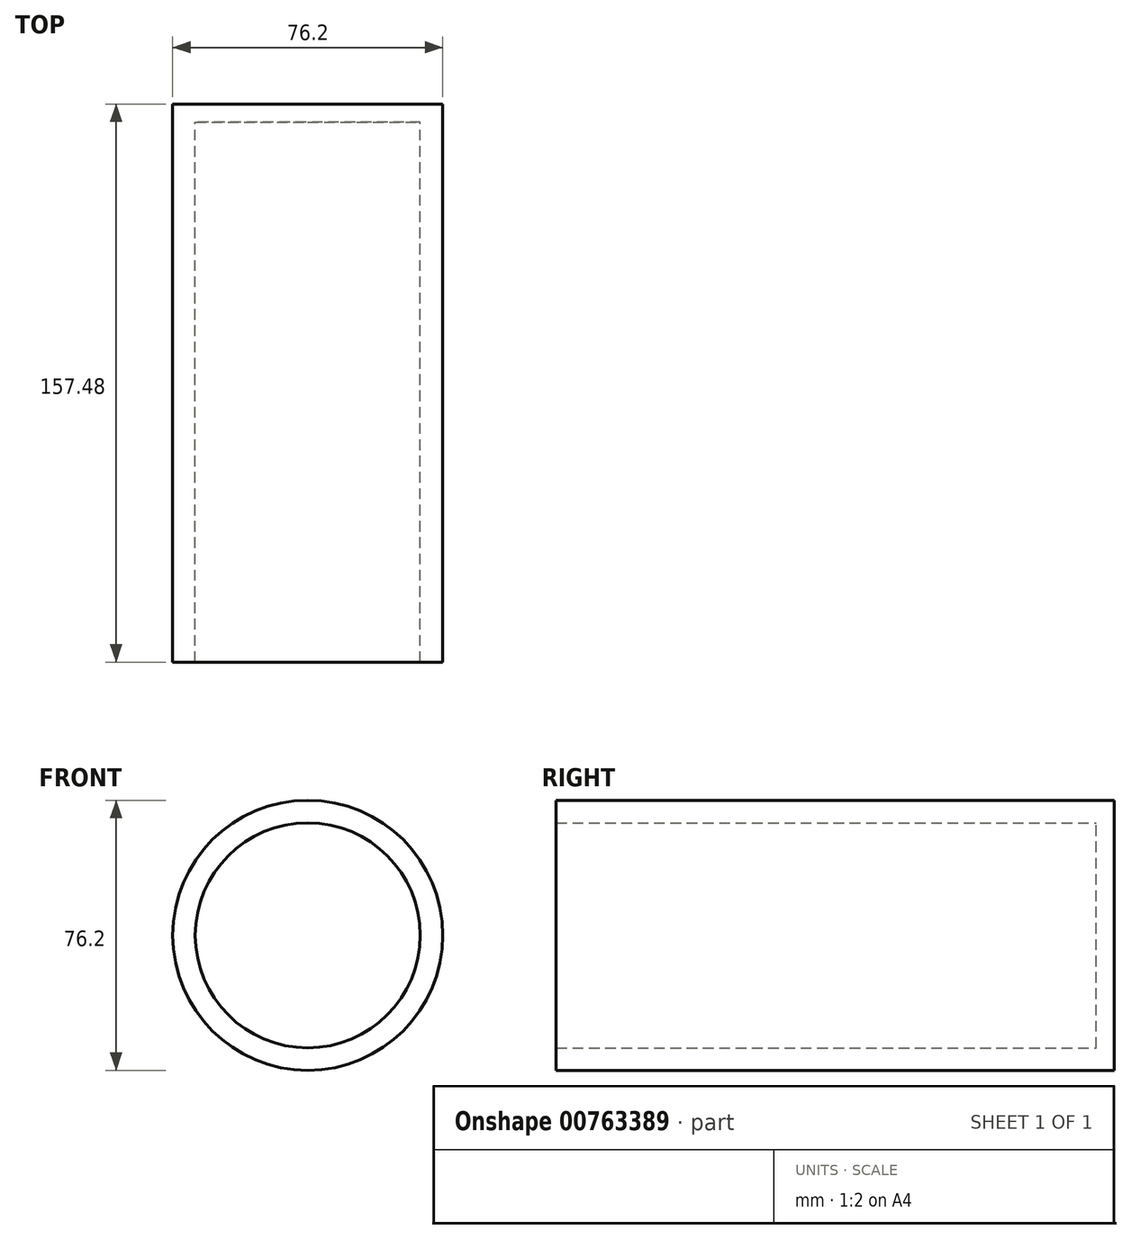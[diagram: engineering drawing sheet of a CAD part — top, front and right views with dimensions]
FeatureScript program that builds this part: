
annotation { "Feature Type Name" : "Feature", "Feature Type Description" : "" }
export const myFeature = defineFeature(function(context is Context, id is Id, definition is map)
    precondition{}
    {
        {
            var Q0;
            Q0=qCreatedBy(makeId("Front.planeOp"),FACE);
            var sketch = newSketch(context, id + "F0", { "sketchPlane" : qUnion([Q0])});
            skCircle(sketch, "E0", {"center": v(0, 0) * mm, "radius": 38.1 * mm});
            skCircle(sketch, "E1", {"center": v(0, 0) * mm, "radius": 31.75 * mm});
            skSolve(sketch);
        }
        {
            var Q0;
            Q0=makeQuery(id+"F0.imprint","IMPRINT",FACE,{"disambiguationData":[TD([[makeQuery(id+"F0.imprint","IMPRINT",EDGE,{"derivedFrom":sQuery(id+"F0.wireOp",EDGE,"E0")}),1.0]])]});
            extrude(context, id + "F1", {"entities" : qUnion([Q0]), "depth" : 152.4 * mm, "offsetDistance" : 25.4 * mm});
        }
        {
            var Q0;
            Q0=makeQuery(id+"F1.opExtrude","CAP_FACE",FACE,{"disambiguationData":[OSD([sQuery(id+"F0.wireOp",EDGE,"E0"),sQuery(id+"F0.wireOp",EDGE,"E1")])],"isStart":true});
            var sketch = newSketch(context, id + "F2", { "sketchPlane" : qUnion([Q0])});
            skCircle(sketch, "E2", {"center": v(0, 0) * mm, "radius": 38.1 * mm});
            skSolve(sketch);
        }
        {
            var Q0;
            Q0=makeQuery(id+"F2.imprint","IMPRINT",FACE,{"disambiguationData":[TD([[makeQuery(id+"F2.imprint","IMPRINT",EDGE,{"derivedFrom":sQuery(id+"F2.wireOp",EDGE,"E2")}),-1.0]])]});
            var Q1;
            Q1=makeQuery(id+"F2.imprint","IMPRINT",FACE,{"disambiguationData":[TD([[makeQuery(id+"F2.imprint","IMPRINT",EDGE,{"derivedFrom":makeQuery(id+"F1.opExtrude","CAP_EDGE",EDGE,{"disambiguationData":[OSD([sQuery(id+"F0.wireOp",EDGE,"E1")])],"isStart":true})}),-1.0]])]});
            extrude(context, id + "F3", {"entities" : qUnion([Q0, Q1]), "operationType" : NewBodyOperationType.ADD, "depth" : 5.08 * mm, "offsetDistance" : 25.4 * mm});
        }
    });
